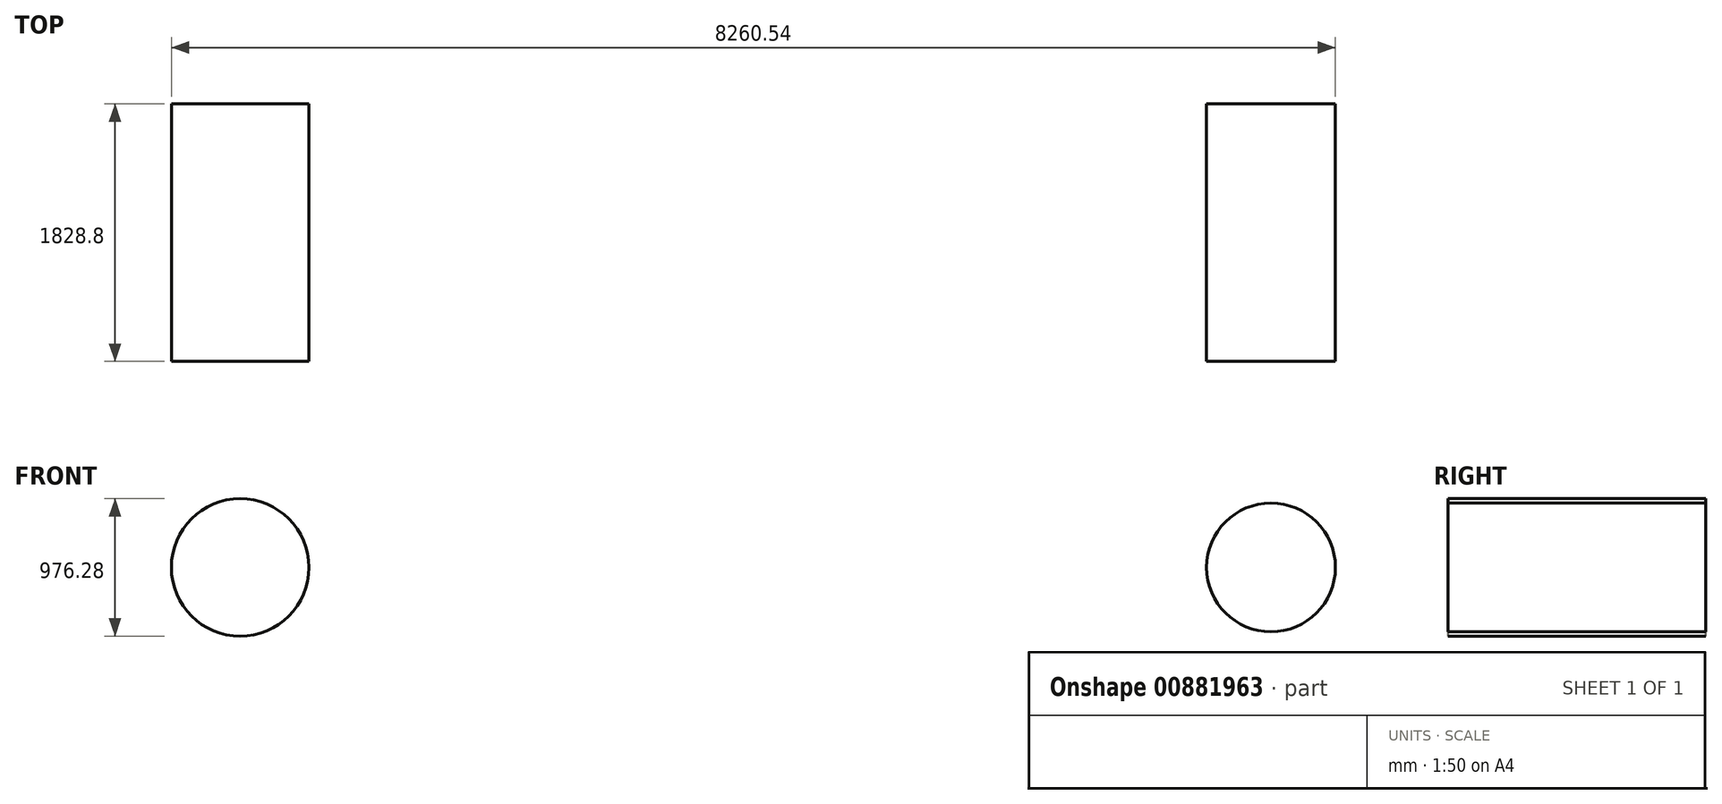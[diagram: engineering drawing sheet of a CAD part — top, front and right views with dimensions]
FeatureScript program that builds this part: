
annotation { "Feature Type Name" : "Feature", "Feature Type Description" : "" }
export const myFeature = defineFeature(function(context is Context, id is Id, definition is map)
    precondition{}
    {
        {
            var Q0;
            Q0=qCreatedBy(makeId("Front.planeOp"),FACE);
            var sketch = newSketch(context, id + "F0", { "sketchPlane" : qUnion([Q0])});
            skCircle(sketch, "E0", {"center": v(0, 0) * mm, "radius": 457.2 * mm});
            skCircle(sketch, "E1", {"center": v(-7315.2, 0) * mm, "radius": 488.14 * mm});
            skSolve(sketch);
        }
        {
            var Q0;
            Q0 = qSketchRegion(id + "F0", true);
            extrude(context, id + "F1", {"entities" : qUnion([Q0]), "depth" : 1828.8 * mm, "offsetDistance" : 25.4 * mm});
        }
    });
